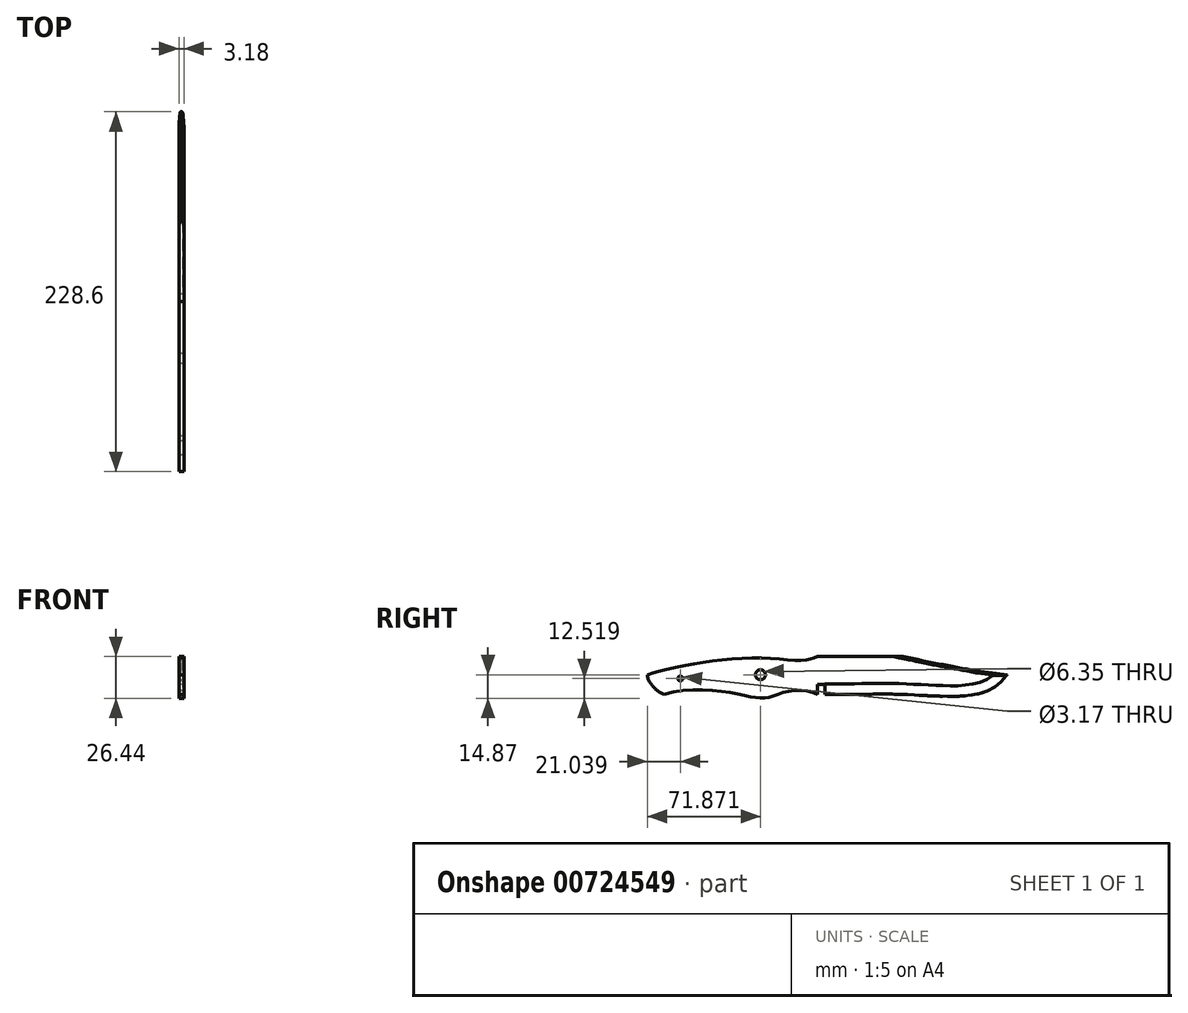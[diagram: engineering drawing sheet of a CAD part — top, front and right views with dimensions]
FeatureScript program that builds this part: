
annotation { "Feature Type Name" : "Feature", "Feature Type Description" : "" }
export const myFeature = defineFeature(function(context is Context, id is Id, definition is map)
    precondition{}
    {
        {
            var Q0;
            Q0=qCreatedBy(makeId("Right.planeOp"),FACE);
            var sketch = newSketch(context, id + "F0", { "sketchPlane" : qUnion([Q0])});
            skLineSegment(sketch, "E0", {"start": v(0, 0) * mm, "end": v(-107.95, 0) * mm, "construction": true});
            skFitSpline(sketch, "E1", {"points": [v(-107.95, 0) * mm, v(-97.47, -12.54) * mm], "startDerivative": vector(0.67, -14.82) * mm, "endDerivative": vector(13.37, -5.48) * mm});
            skFitSpline(sketch, "E2", {"points": [v(-107.95, 0) * mm, v(-86.96, 5.28) * mm, v(-40.4, 10.7) * mm, v(-7.57, 9.28) * mm, v(0, 11.57) * mm], "startDerivative": vector(83.14, 28.46) * mm, "endDerivative": vector(44.55, 19.45) * mm});
            skFitSpline(sketch, "E3", {"points": [v(0, -12.54) * mm, v(-19.28, -10.7) * mm, v(-32.7, -14.7) * mm, v(-49, -12.54) * mm, v(-97.47, -12.54) * mm], "startDerivative": vector(-61.47, 37.4) * mm, "endDerivative": vector(-135.83, -44.52) * mm});
            skLineSegment(sketch, "E4.top", {"start": v(0, -6.19) * mm, "end": v(4.76, -6.19) * mm});
            skLineSegment(sketch, "E4.left", {"start": v(0, -12.54) * mm, "end": v(0, -6.19) * mm});
            skLineSegment(sketch, "E4.right", {"start": v(4.76, -12.54) * mm, "end": v(4.76, -6.19) * mm});
            skLineSegment(sketch, "E5", {"start": v(0, 11.57) * mm, "end": v(4.76, 11.57) * mm});
            skLineSegment(sketch, "E6", {"start": v(0, 0) * mm, "end": v(120.65, 0) * mm, "construction": true});
            skLineSegment(sketch, "E7", {"start": v(4.76, -12.54) * mm, "end": v(4.76, -12.54) * mm});
            skFitSpline(sketch, "E8", {"points": [v(4.76, -12.54) * mm, v(55.99, -12.54) * mm, v(100.25, -12.54) * mm, v(120.65, 0) * mm], "startDerivative": vector(181.9, -0.8) * mm, "endDerivative": vector(58.16, 78.94) * mm});
            skFitSpline(sketch, "E9", {"points": [v(4.76, 11.57) * mm, v(54.3, 11.57) * mm], "startDerivative": vector(49.54, 0) * mm, "endDerivative": vector(49.54, 0) * mm});
            skFitSpline(sketch, "E10", {"points": [v(54.3, 11.57) * mm, v(120.65, 0) * mm, v(144.6, 0) * mm], "startDerivative": vector(119, -24.24) * mm, "endDerivative": vector(56.3, 3.45) * mm});
            skFitSpline(sketch, "E11.0", {"points": [v(4.75, -16.1) * mm, v(12.35, -16.12) * mm, v(22.02, -16.04) * mm, v(32.87, -15.9) * mm, v(40.36, -15.82) * mm, v(46.36, -15.84) * mm, v(51.2, -15.93) * mm, v(54.28, -16.03) * mm, v(56.8, -16.13) * mm, v(59.39, -16.25) * mm, v(62.69, -16.42) * mm, v(66.74, -16.64) * mm, v(72.22, -16.94) * mm, v(79.15, -17.24) * mm, v(87.32, -17.33) * mm, v(93.81, -17.02) * mm, v(98.72, -16.44) * mm, v(103.4, -15.6) * mm, v(108.75, -14) * mm, v(114.43, -11.09) * mm, v(119.37, -7.17) * mm, v(122.2, -3.9) * mm, v(123.51, -2.1) * mm]});
            skCircle(sketch, "E12", {"center": v(-36.08, 0) * mm, "radius": 3.18 * mm});
            skCircle(sketch, "E13", {"center": v(-86.91, -2.35) * mm, "radius": 1.59 * mm});
            skSolve(sketch);
        }
        {
            var Q0;
            Q0 = qSketchRegion(id + "F0", true);
            extrude(context, id + "F1", {"entities" : qUnion([Q0]), "endBound" : BoundingType.SYMMETRIC, "depth" : 3.17 * mm, "offsetDistance" : 25.4 * mm});
        }
        {
            var Q0;
            Q0=qCreatedBy(makeId("Front.planeOp"),FACE);
            cPlane(context, id + "F2", {"entities" : qUnion([Q0]), "cplaneType" : CPlaneType.OFFSET, "offset" : 4.76 * mm, "oppositeDirection" : true, "width" : 152.4 * mm, "height" : 152.4 * mm});
        }
        {
            var Q0;
            Q0=qCreatedBy(id+"F2.planeOp",FACE);
            var sketch = newSketch(context, id + "F3", { "sketchPlane" : qUnion([Q0])});
            skLineSegment(sketch, "E14", {"start": v(-2, -1.87) * mm, "end": v(-0.25, -18.42) * mm});
            skLineSegment(sketch, "E15", {"start": v(-0.25, -18.42) * mm, "end": v(-2, -18.42) * mm});
            skLineSegment(sketch, "E16", {"start": v(-2, -18.42) * mm, "end": v(-2, -1.87) * mm});
            skLineSegment(sketch, "E17.MirrorCS", {"start": v(2, -1.87) * mm, "end": v(0.25, -18.42) * mm});
            skLineSegment(sketch, "E18.MirrorCS", {"start": v(0.25, -18.42) * mm, "end": v(2, -18.42) * mm});
            skLineSegment(sketch, "E19.MirrorCS", {"start": v(2, -18.42) * mm, "end": v(2, -1.87) * mm});
            skSolve(sketch);
        }
        {
            var Q0;
            Q0=makeQuery(id+"F3.imprint","IMPRINT",FACE,{"disambiguationData":[TD([[makeQuery(id+"F3.imprint","IMPRINT",EDGE,{"derivedFrom":sQuery(id+"F3.wireOp",EDGE,"E14")}),-1.0]])]});
            var Q1;
            Q1=makeQuery(id+"F3.imprint","IMPRINT",FACE,{"disambiguationData":[TD([[makeQuery(id+"F3.imprint","IMPRINT",EDGE,{"derivedFrom":sQuery(id+"F3.wireOp",EDGE,"E17.MirrorCS")}),1.0]])]});
            var Q2;
            Q2=sQuery(id+"F0.wireOp",EDGE,"E11.0");
            sweep(context, id + "F4", {"operationType" : NewBodyOperationType.REMOVE, "profiles" : qUnion([Q0, Q1]), "path" : qUnion([Q2])});
        }
        {
            var Q0;
            {var subQ0=sQuery(id+"F0.wireOp",EDGE,"E10");var subQ1=sQuery(id+"F0.wireOp",EDGE,"E9");Q0=makeQuery(id+"F4.boolean.opBoolean","SPLIT",EDGE,{"disambiguationData":[TD([makeQuery(id+"F1.opExtrude","SWEPT_FACE",FACE,{"disambiguationData":[OSD([subQ1])]})])],"derivedFrom":makeQuery(id+"F1.opExtrude","CAP_EDGE",EDGE,{"disambiguationData":[OSD([subQ0])],"isStart":false})});}
            var Q1;
            {var subQ0=sQuery(id+"F0.wireOp",EDGE,"E10");var subQ1=sQuery(id+"F0.wireOp",EDGE,"E9");Q1=makeQuery(id+"F4.boolean.opBoolean","SPLIT",EDGE,{"disambiguationData":[TD([makeQuery(id+"F1.opExtrude","SWEPT_FACE",FACE,{"disambiguationData":[OSD([subQ1])]})])],"derivedFrom":makeQuery(id+"F1.opExtrude","CAP_EDGE",EDGE,{"disambiguationData":[OSD([subQ0])],"isStart":true})});}
            chamfer(context, id + "F5", {"entities" : qUnion([Q0, Q1]), "width" : 1.27 * mm, "tangentPropagation" : true});
        }
    });
